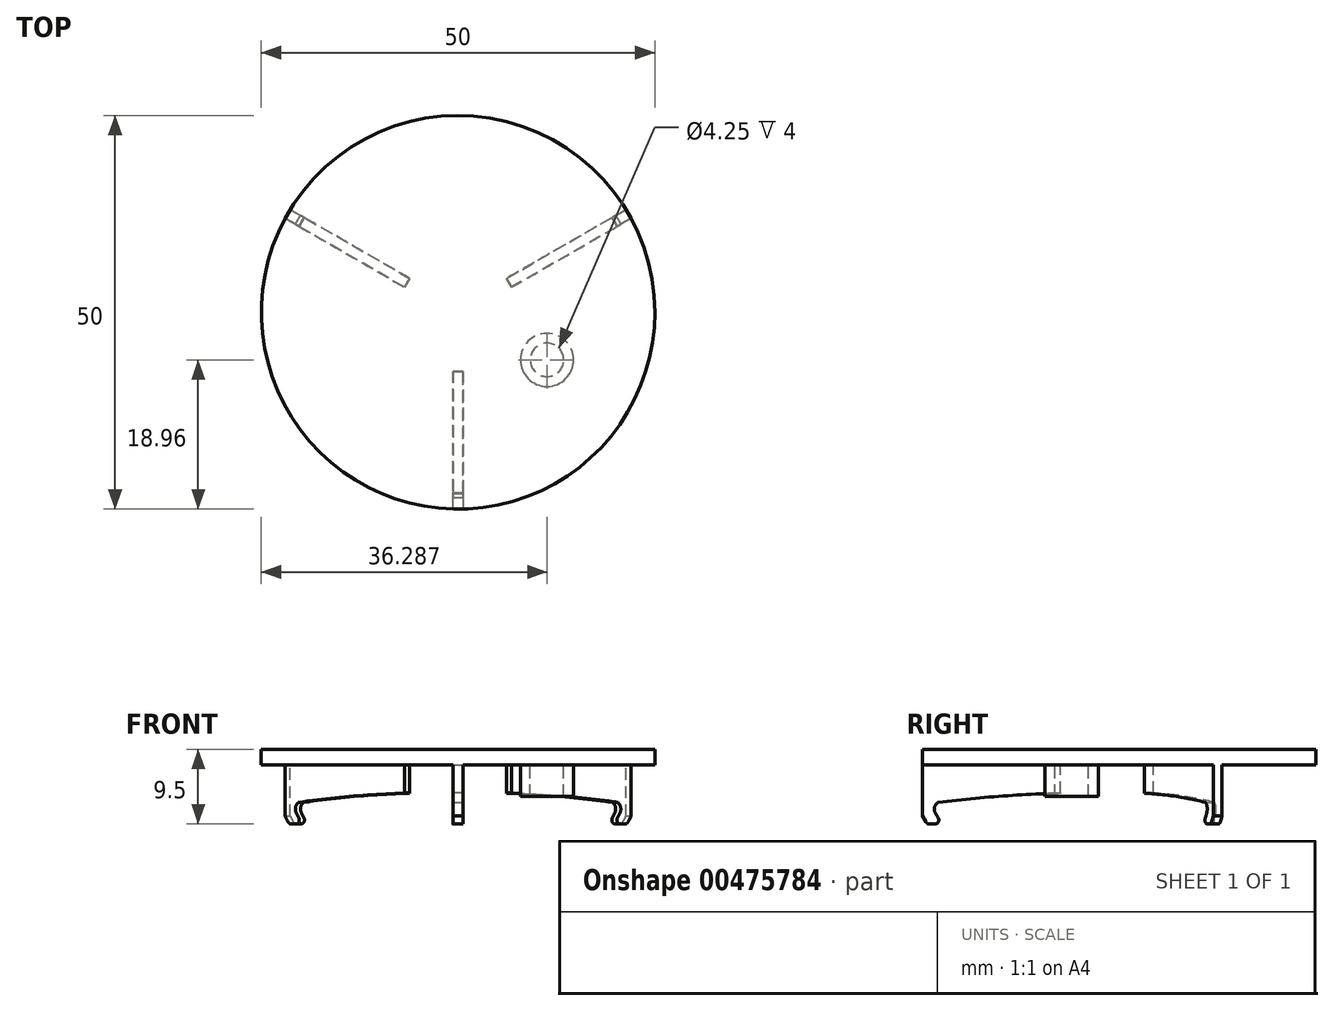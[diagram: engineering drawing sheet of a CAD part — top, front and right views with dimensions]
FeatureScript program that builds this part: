
annotation { "Feature Type Name" : "Feature", "Feature Type Description" : "" }
export const myFeature = defineFeature(function(context is Context, id is Id, definition is map)
    precondition{}
    {
        {
            var Q0;
            Q0=qCreatedBy(makeId("Top.planeOp"),FACE);
            var sketch = newSketch(context, id + "F0", { "sketchPlane" : qUnion([Q0])});
            skCircle(sketch, "E0", {"center": v(0, 0) * mm, "radius": 25 * mm});
            skSolve(sketch);
        }
        {
            var Q0;
            Q0 = qSketchRegion(id + "F0", true);
            extrude(context, id + "F1", {"entities" : qUnion([Q0]), "depth" : 2 * mm});
        }
        {
            var Q0;
            Q0=makeQuery(id+"F1.opExtrude","CAP_FACE",FACE,{"disambiguationData":[OSD([sQuery(id+"F0.wireOp",EDGE,"E0")])],"isStart":true});
            var sketch = newSketch(context, id + "F2", { "sketchPlane" : qUnion([Q0])});
            skLineSegment(sketch, "E1", {"start": v(0, 0) * mm, "end": v(0, 35.27) * mm, "construction": true});
            skLineSegment(sketch, "E2", {"start": v(-0.65, 25) * mm, "end": v(-0.65, 7.5) * mm});
            skLineSegment(sketch, "E3", {"start": v(-0.65, 7.5) * mm, "end": v(0.65, 7.5) * mm});
            skLineSegment(sketch, "E4", {"start": v(0.65, 7.5) * mm, "end": v(0.65, 25) * mm});
            skArc(sketch, "E5", {"start": v(0.65, 25) * mm, "mid": v(0, 25) * mm, "end": v(-0.65, 25) * mm});
            skSolve(sketch);
        }
        {
            var Q0;
            Q0 = qSketchRegion(id + "F2", true);
            extrude(context, id + "F3", {"entities" : qUnion([Q0]), "operationType" : NewBodyOperationType.ADD, "depth" : 5 * mm});
        }
        {
            var Q0;
            Q0=makeQuery(id+"F1.opExtrude","SWEPT_BODY",BODY,{"disambiguationData":[OSD([sQuery(id+"F0.wireOp",EDGE,"E0")])]});
            var Q1;
            Q1=makeQuery(id+"F3.boolean.opBoolean","MERGE",FACE,{"derivedFrom":[makeQuery(id+"F1.opExtrude","SWEPT_FACE",FACE,{"disambiguationData":[OSD([sQuery(id+"F0.wireOp",EDGE,"E0")])]}),makeQuery(id+"F3.opExtrude","SWEPT_FACE",FACE,{"disambiguationData":[OSD([sQuery(id+"F2.wireOp",EDGE,"E5")])]})]});
            circularPattern(context, id + "F4", {"operationType" : NewBodyOperationType.ADD, "entities" : qUnion([Q0]), "axis" : qUnion([Q1]), "angle" : 360 * degree, "instanceCount" : 3, "equalSpace" : true});
        }
        {
            var Q0;
            Q0=qCreatedBy(makeId("Right.planeOp"),FACE);
            var sketch = newSketch(context, id + "F5", { "sketchPlane" : qUnion([Q0])});
            skLineSegment(sketch, "E6.1", {"start": v(-7.5, -5) * mm, "end": v(-7.5, -3.58) * mm});
            skPoint(sketch, "E7.orphan", {"position": v(0, -3.53) * mm});
            skPoint(sketch, "E8.orphan", {"position": v(-7.5, 0) * mm});
            skLineSegment(sketch, "E9.0", {"start": v(-25, -5) * mm, "end": v(-7.5, -5) * mm});
            skArc(sketch, "E10", {"start": v(-7.5, -3.58) * mm, "mid": v(-16.26, -4.06) * mm, "end": v(-25, -5) * mm});
            skLineSegment(sketch, "E11", {"start": v(0, 0) * mm, "end": v(0, 12.27) * mm, "construction": true});
            skSolve(sketch);
        }
        {
            var Q0;
            Q0 = qSketchRegion(id + "F5", true);
            var Q1;
            Q1=sQuery(id+"F5.wireOp",EDGE,"E11");
            revolve(context, id + "F6", {"operationType" : NewBodyOperationType.REMOVE, "entities" : qUnion([Q0]), "axis" : qUnion([Q1]), "revolveType" : RevolveType.FULL, "oppositeDirection" : true});
        }
        {
            var Q0;
            Q0=qCreatedBy(makeId("Right.planeOp"),FACE);
            var sketch = newSketch(context, id + "F7", { "sketchPlane" : qUnion([Q0])});
            skLineSegment(sketch, "E12", {"start": v(-25, -4.62) * mm, "end": v(-25, -6.5) * mm});
            skLineSegment(sketch, "E13", {"start": v(-25, -6.5) * mm, "end": v(-24.57, -7.25) * mm});
            skLineSegment(sketch, "E14", {"start": v(-24.13, -7.5) * mm, "end": v(-23.43, -7.5) * mm});
            skLineSegment(sketch, "E15", {"start": v(-23, -6.75) * mm, "end": v(-23.37, -6.1) * mm});
            skArc(sketch, "E16.filletArc", {"start": v(-22.66, -4.62) * mm, "mid": v(-23.4, -5.17) * mm, "end": v(-23.37, -6.1) * mm});
            skPoint(sketch, "E17.orphan", {"position": v(-7.5, -3.58) * mm});
            skPoint(sketch, "E18.visualSharp", {"position": v(-24.42, -7.5) * mm});
            skArc(sketch, "E18.filletArc", {"start": v(-24.57, -7.25) * mm, "mid": v(-24.38, -7.43) * mm, "end": v(-24.13, -7.5) * mm});
            skPoint(sketch, "E19.visualSharp", {"position": v(-22.56, -7.5) * mm});
            skArc(sketch, "E19.filletArc", {"start": v(-23.43, -7.5) * mm, "mid": v(-23, -7.25) * mm, "end": v(-23, -6.75) * mm});
            skLineSegment(sketch, "E20", {"start": v(0, 0) * mm, "end": v(0, 9.15) * mm, "construction": true});
            skLineSegment(sketch, "E21", {"start": v(-22.66, -4.62) * mm, "end": v(-25, -4.62) * mm});
            skSolve(sketch);
        }
        {
            var Q0;
            Q0=makeQuery(id+"F7.imprint","IMPRINT",FACE,{"disambiguationData":[TD([[makeQuery(id+"F7.imprint","IMPRINT",EDGE,{"derivedFrom":sQuery(id+"F7.wireOp",EDGE,"E12")}),1.0]])]});
            var Q1;
            Q1=sQuery(id+"F7.wireOp",EDGE,"E20");
            revolve(context, id + "F8", {"operationType" : NewBodyOperationType.ADD, "entities" : qUnion([Q0]), "axis" : qUnion([Q1]), "revolveType" : RevolveType.FULL});
        }
        {
            var Q0;
            Q0=makeQuery(id+"F8.opRevolve","SWEPT_FACE",FACE,{"disambiguationData":[OSD([sQuery(id+"F7.wireOp",EDGE,"E21")])]});
            extrude(context, id + "F9", {"entities" : qUnion([Q0]), "operationType" : NewBodyOperationType.REMOVE, "oppositeDirection" : true, "depth" : 25 * mm});
        }
        {
            var Q0;
            Q0=makeQuery(id+"F1.opExtrude","CAP_FACE",FACE,{"disambiguationData":[OSD([sQuery(id+"F0.wireOp",EDGE,"E0")])],"isStart":true});
            var sketch = newSketch(context, id + "F10", { "sketchPlane" : qUnion([Q0])});
            skCircle(sketch, "E22", {"center": v(11.29, 6.04) * mm, "radius": 2.12 * mm});
            skCircle(sketch, "E23", {"center": v(11.29, 6.04) * mm, "radius": 3.37 * mm});
            skSolve(sketch);
        }
        {
            var Q0;
            Q0 = qSketchRegion(id + "F10", true);
            extrude(context, id + "F11", {"entities" : qUnion([Q0]), "operationType" : NewBodyOperationType.ADD, "depth" : 4 * mm, "offsetDistance" : 25 * mm});
        }
    });
